FCSTD DOCUMENT  (FreeCAD 0.19R)
Label: base_dimensions
License: Creative Commons Attribution-ShareAlike
LicenseURL: http://creativecommons.org/licenses/by-sa/4.0/
objects: Sketcher::SketchObject×4, PartDesign::Body×1, App::Part×1
note: 5 computed .brp shape members not serialized (recipe doc carries the construction recipe); baked Part::Feature solids carry a one-line shape summary decoded from their .brp

FEATURE [Sketcher::SketchObject] Sketch  label="inside_line"
  MapMode = 5
  Placement = pos=(0,0,0) rot=(1,0,0;1.5708rad)
  Support = -> [XZ_Plane001]
  sketch-geometry (14):
    g0: LineSegment StartX=-90 StartY=140 StartZ=0 EndX=90 EndY=140 EndZ=0
    g1: LineSegment StartX=90 StartY=140 StartZ=0 EndX=5 EndY=10 EndZ=0
    g2: LineSegment [constr] StartX=5 StartY=10 StartZ=0 EndX=-5 EndY=10 EndZ=0
    g3: LineSegment StartX=-5 StartY=10 StartZ=0 EndX=-90 EndY=140 EndZ=0
    g4: LineSegment StartX=5 StartY=10 StartZ=0 EndX=5 EndY=0 EndZ=0
    g5: LineSegment StartX=-5 StartY=10 StartZ=0 EndX=-5 EndY=0 EndZ=0
    g6: LineSegment [constr] StartX=-5 StartY=0 StartZ=0 EndX=5 EndY=0 EndZ=0
    g7: LineSegment StartX=-5 StartY=0 StartZ=0 EndX=-5 EndY=-10 EndZ=0
    g8: LineSegment StartX=-5 StartY=-10 StartZ=0 EndX=-90 EndY=-140 EndZ=0
    g9: LineSegment StartX=-90 StartY=-140 StartZ=0 EndX=90 EndY=-140 EndZ=0
    g10: LineSegment StartX=90 StartY=-140 StartZ=0 EndX=5 EndY=-10 EndZ=0
    g11: LineSegment StartX=5 StartY=-10 StartZ=0 EndX=5 EndY=0 EndZ=0
    g12: LineSegment [constr] StartX=90 StartY=140 StartZ=0 EndX=90 EndY=0 EndZ=0
    g13: LineSegment [constr] StartX=90 StartY=0 StartZ=0 EndX=90 EndY=-140 EndZ=0
  constraints (38):
    c: Horizontal(g0)
    c: Coincident(g0,g1)
    c: Coincident(g1,g2)
    c: Horizontal(g2)
    c: Coincident(g2,g3)
    c: Coincident(g0,g3)
    c: Equal(g3,g1)
    c: Coincident(g4,g1)
    c: PointOnObject(g4,g-1)
    c: Vertical(g4)
    c: Coincident(g5,g3)
    c: Vertical(g5)
    c: Coincident(g6,g4)
    c: Coincident(g5,g6)
    c: Symmetric(g6,g6,g-1)
    c: DistanceX(g2,g2) = 10  'slot_width'
    c: DistanceX(g0,g0) = 180  'width'
    c: DistanceY(g4,g4) = 10
    c: Vertical(g7)
    c: Coincident(g7,g8)
    c: Coincident(g8,g9)
    c: Horizontal(g9)
    c: Coincident(g9,g10)
    c: Coincident(g10,g11)
    c: Vertical(g11)
    c: Coincident(g4,g11)
    c: Coincident(g5,g7)
    c: Equal(g11,g7)
    c: Equal(g7,g5)
    c: Equal(g9,g0)
    c: Coincident(g0,g12)
    c: Vertical(g12)
    c: Coincident(g12,g13)
    c: Vertical(g13)
    c: Coincident(g13,g9)
    c: PointOnObject(g12,g-1)
    c: Equal(g12,g13)
    c: DistanceY(g9,g0) = 280  'height'
FEATURE [Sketcher::SketchObject] Sketch001  label="frame"
  ExternalGeometry = -> [Sketch]
  MapMode = 5
  Placement = pos=(0,0,0) rot=(1,0,0;1.5708rad)
  Support = -> [XZ_Plane001]
  sketch-geometry (17):
    g0: LineSegment StartX=-6 StartY=5 StartZ=0 EndX=-5 EndY=10 EndZ=0
    g1: LineSegment StartX=-5 StartY=10 StartZ=0 EndX=-90 EndY=140 EndZ=0
    g2: LineSegment StartX=-90 StartY=140 StartZ=0 EndX=90 EndY=140 EndZ=0
    g3: LineSegment StartX=90 StartY=140 StartZ=0 EndX=5 EndY=10 EndZ=0
    g4: LineSegment StartX=5 StartY=10 StartZ=0 EndX=6 EndY=5 EndZ=0
    g5: LineSegment StartX=9 StartY=6.98104 StartZ=0 EndX=95.9739 EndY=140 EndZ=0
    g6: LineSegment StartX=95.9739 StartY=140 StartZ=0 EndX=95.9739 EndY=145 EndZ=0
    g7: LineSegment StartX=95.9739 StartY=145 StartZ=0 EndX=-95.9739 EndY=145 EndZ=0
    g8: LineSegment StartX=-95.9739 StartY=145 StartZ=0 EndX=-95.9739 EndY=140 EndZ=0
    g9: LineSegment StartX=-95.9739 StartY=140 StartZ=0 EndX=-9 EndY=6.98104 EndZ=0
    g10: LineSegment StartX=-9 StartY=6.98104 StartZ=0 EndX=-9 EndY=5 EndZ=0
    g11: LineSegment StartX=-9 StartY=5 StartZ=0 EndX=-6 EndY=5 EndZ=0
    g12: LineSegment StartX=6 StartY=5 StartZ=0 EndX=9 EndY=5 EndZ=0
    g13: LineSegment StartX=9 StartY=5 StartZ=0 EndX=9 EndY=6.98104 EndZ=0
    g14: LineSegment [constr] StartX=-6 StartY=5 StartZ=0 EndX=6 EndY=5 EndZ=0
    g15: GeomPoint X=0 Y=5 Z=0
    g16: LineSegment [constr] StartX=-9 StartY=6.98104 StartZ=0 EndX=-4.81515 EndY=9.71729 EndZ=0
  constraints (44):
    c: Coincident(g0,g-4)
    c: Coincident(g0,g1)
    c: Coincident(g1,g-3)
    c: Coincident(g1,g2)
    c: Coincident(g2,g-3)
    c: Coincident(g2,g3)
    c: Coincident(g3,g-5)
    c: Coincident(g3,g4)
    c: Coincident(g5,g6)
    c: Vertical(g6)
    c: Coincident(g6,g7)
    c: Horizontal(g7)
    c: Coincident(g7,g8)
    c: Vertical(g8)
    c: Coincident(g8,g9)
    c: Coincident(g9,g10)
    c: Vertical(g10)
    c: Coincident(g10,g11)
    c: Coincident(g11,g0)
    c: Horizontal(g11)
    c: Coincident(g4,g12)
    c: Horizontal(g12)
    c: Coincident(g12,g13)
    c: Vertical(g13)
    c: Coincident(g5,g13)
    c: Equal(g13,g10)
    c: Equal(g11,g12)
    c: DistanceX(g12,g12) = 3
    c: Horizontal(g14)
    c: Coincident(g4,g14)
    c: Coincident(g0,g14)
    c: Symmetric(g14,g14,g15)
    c: PointOnObject(g15,g-2)
    c: DistanceY(g15) = 5  'offset'
    c: DistanceX(g3,g4) = 1
    c: Parallel(g5,g3)
    c: Parallel(g9,g1)
    c: PointOnObject(g8,g2)
    c: PointOnObject(g5,g2)
    c: Coincident(g16,g9)
    c: PointOnObject(g16,g1)
    c: Perpendicular(g16,g1)
    c: Distance(g16) = 5
    c: Equal(g16,g8)
FEATURE [Sketcher::SketchObject] Sketch002  label="thickness"
  MapMode = 5
  Placement = pos=(0,0,0) rot=(0.57735,0.57735,0.57735;2.0944rad)
  Support = -> [YZ_Plane001]
  sketch-geometry (3):
    g0: LineSegment StartX=-2.5 StartY=0 StartZ=0 EndX=2.5 EndY=0 EndZ=0
    g1: LineSegment StartX=-2.5 StartY=0 StartZ=0 EndX=-4.5 EndY=0 EndZ=0
    g2: LineSegment StartX=-4.5 StartY=0 StartZ=0 EndX=-5.5 EndY=0 EndZ=0
  constraints (9):
    c: Horizontal(g0)
    c: Symmetric(g0,g0,g-1)
    c: DistanceX(g0,g0) = 5  'center'
    c: Coincident(g1,g0)
    c: Horizontal(g1)
    c: DistanceX(g1,g1) = 2  'glass'
    c: Coincident(g2,g1)
    c: Horizontal(g2)
    c: DistanceX(g2,g2) = 1  'cover'
FEATURE [Sketcher::SketchObject] Sketch003  label="glass_outline"
  ExternalGeometry = -> [Sketch001]
  MapMode = 5
  Placement = pos=(0,0,0) rot=(1,0,0;1.5708rad)
  Support = -> [XZ_Plane001]
  sketch-geometry (6):
    g0: LineSegment StartX=-99.2432 StartY=145 StartZ=0 EndX=99.2432 EndY=145 EndZ=0
    g1: LineSegment StartX=99.2432 StartY=145 StartZ=0 EndX=9 EndY=6.98104 EndZ=0
    g2: LineSegment StartX=9 StartY=6.98104 StartZ=0 EndX=9 EndY=5 EndZ=0
    g3: LineSegment StartX=9 StartY=5 StartZ=0 EndX=-9 EndY=5 EndZ=0
    g4: LineSegment StartX=-9 StartY=5 StartZ=0 EndX=-9 EndY=6.98104 EndZ=0
    g5: LineSegment StartX=-9 StartY=6.98104 StartZ=0 EndX=-99.2432 EndY=145 EndZ=0
  constraints (14):
    c: Horizontal(g0)
    c: Coincident(g0,g1)
    c: Coincident(g1,g2)
    c: Coincident(g2,g3)
    c: Coincident(g3,g4)
    c: Coincident(g4,g5)
    c: Coincident(g5,g0)
    c: Coincident(g2,g-6)
    c: Coincident(g3,g-7)
    c: Coincident(g4,g-3)
    c: Coincident(g1,g-5)
    c: PointOnObject(g0,g-3)
    c: PointOnObject(g0,g-5)
    c: PointOnObject(g0,g-4)
FEATURE [PartDesign::Body] Body  label="base_dimensions_Body"
  Group = -> [Sketch,Sketch001,Sketch002,Sketch003]
  Origin = -> Origin001
FEATURE [App::Part] Part  label="base_dimensions"
  Group = -> [Body]
  Origin = -> Origin
